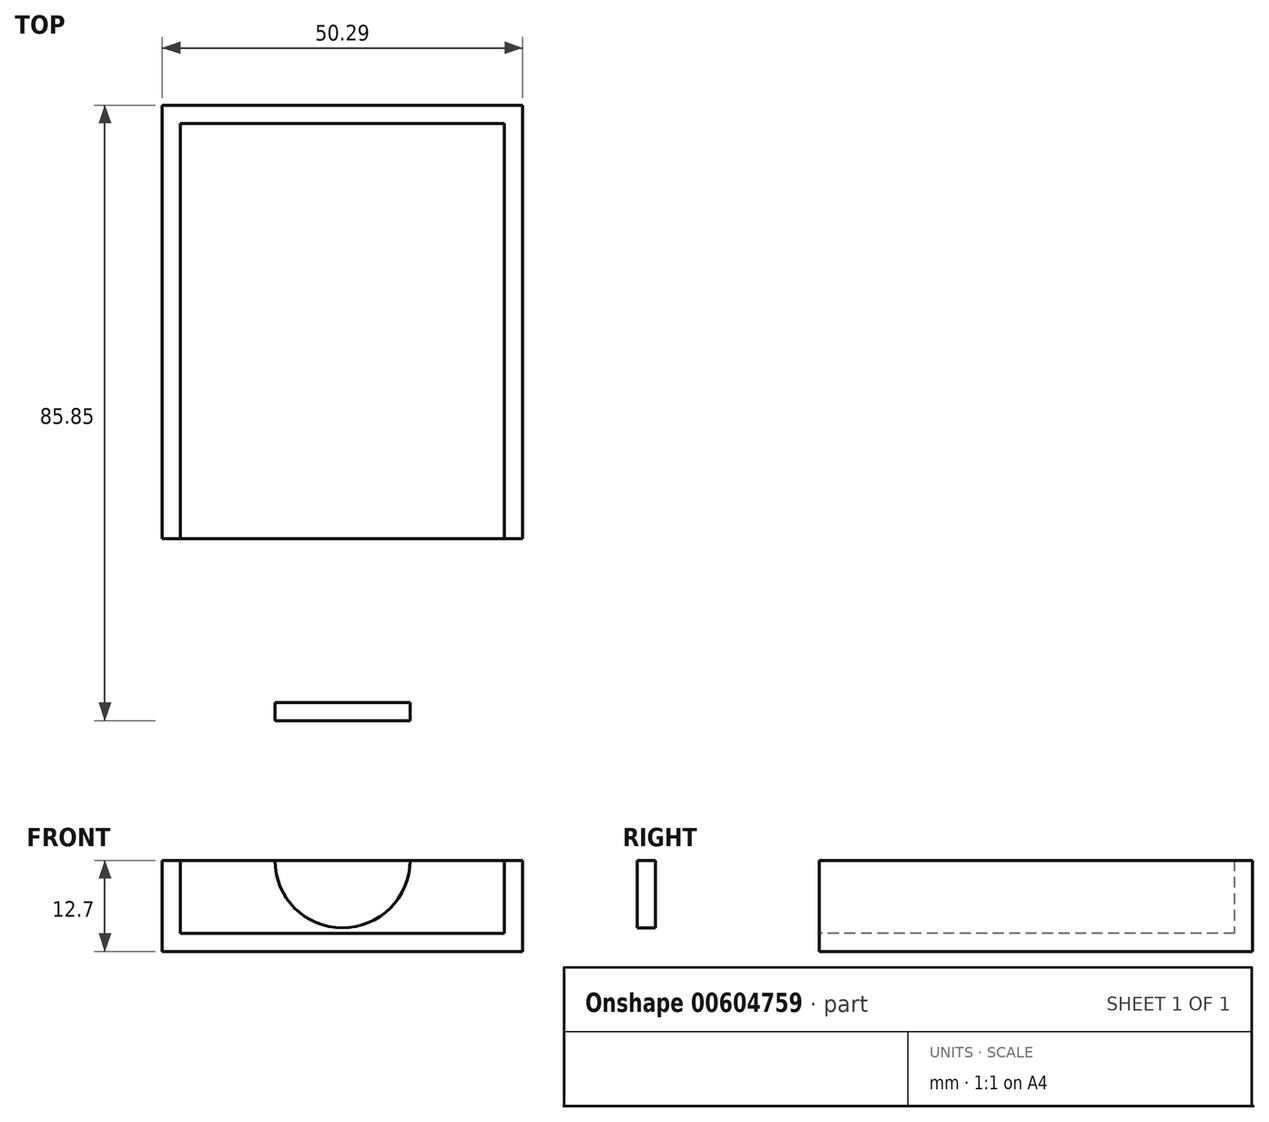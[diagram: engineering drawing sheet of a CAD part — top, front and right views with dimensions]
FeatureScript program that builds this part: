
annotation { "Feature Type Name" : "Feature", "Feature Type Description" : "" }
export const myFeature = defineFeature(function(context is Context, id is Id, definition is map)
    precondition{}
    {
        {
            var Q0;
            Q0=qCreatedBy(makeId("Top.planeOp"),FACE);
            var sketch = newSketch(context, id + "F0", { "sketchPlane" : qUnion([Q0])});
            skLineSegment(sketch, "E0.bottom", {"start": v(0, 0) * mm, "end": v(50.3, 0) * mm});
            skLineSegment(sketch, "E0.top", {"start": v(0, -85.85) * mm, "end": v(50.3, -85.85) * mm});
            skLineSegment(sketch, "E0.left", {"start": v(0, 0) * mm, "end": v(0, -85.85) * mm});
            skLineSegment(sketch, "E0.right", {"start": v(50.3, 0) * mm, "end": v(50.3, -85.85) * mm});
            skSolve(sketch);
        }
        {
            var Q0;
            Q0=makeQuery(id+"F0.imprint","IMPRINT",FACE,{"disambiguationData":[TD([[makeQuery(id+"F0.imprint","IMPRINT",EDGE,{"derivedFrom":sQuery(id+"F0.wireOp",EDGE,"E0.bottom")}),-1.0]])]});
            extrude(context, id + "F1", {"entities" : qUnion([Q0]), "depth" : 12.7 * mm, "offsetDistance" : 25.4 * mm});
        }
        {
            var Q0;
            Q0=makeQuery(id+"F1.opExtrude","CAP_FACE",FACE,{"disambiguationData":[OSD([sQuery(id+"F0.wireOp",EDGE,"E0.bottom"),sQuery(id+"F0.wireOp",EDGE,"E0.top"),sQuery(id+"F0.wireOp",EDGE,"E0.left"),sQuery(id+"F0.wireOp",EDGE,"E0.right")])],"isStart":false});
            shell(context, id + "F2", {"entities" : qUnion([Q0]), "thickness" : 2.54 * mm});
        }
        {
            var Q0;
            Q0=makeQuery(id+"F1.opExtrude","SWEPT_FACE",FACE,{"disambiguationData":[OSD([sQuery(id+"F0.wireOp",EDGE,"E0.top")])]});
            var sketch = newSketch(context, id + "F3", { "sketchPlane" : qUnion([Q0])});
            skArc(sketch, "E1", {"start": v(34.57, 12.7) * mm, "mid": v(25.15, 3.27) * mm, "end": v(15.72, 12.7) * mm});
            skSolve(sketch);
        }
        {
            var Q0;
            {var subQ0=sQuery(id+"F3.wireOp",EDGE,"E1");Q0=makeQuery(id+"F3.imprint","IMPRINT",FACE,{"disambiguationData":[TD([[makeQuery(id+"F3.imprint","IMPRINT",EDGE,{"derivedFrom":subQ0}),-1.0]])]});}
            extrude(context, id + "F4", {"entities" : qUnion([Q0]), "operationType" : NewBodyOperationType.REMOVE, "oppositeDirection" : true, "depth" : 25.4 * mm, "offsetDistance" : 25.4 * mm});
        }
    });
